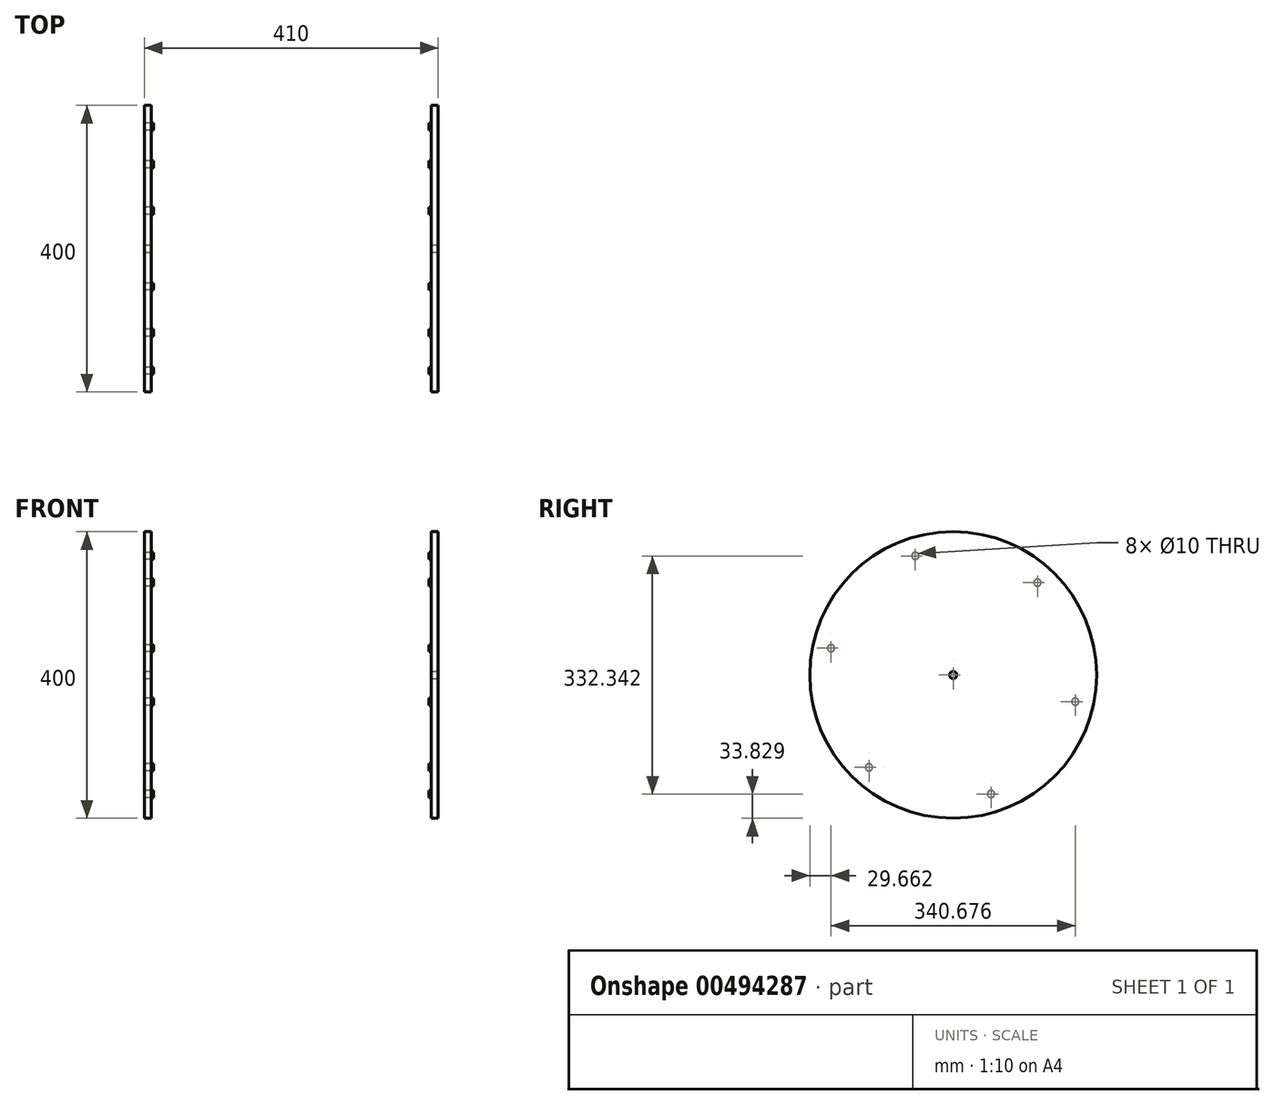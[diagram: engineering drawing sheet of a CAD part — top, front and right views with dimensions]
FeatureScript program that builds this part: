
annotation { "Feature Type Name" : "Feature", "Feature Type Description" : "" }
export const myFeature = defineFeature(function(context is Context, id is Id, definition is map)
    precondition{}
    {
        {
            var Q0;
            Q0=qCreatedBy(makeId("Right.planeOp"),FACE);
            var sketch = newSketch(context, id + "F0", { "sketchPlane" : qUnion([Q0])});
            skCircle(sketch, "E0", {"center": v(0, 0) * mm, "radius": 200 * mm});
            skCircle(sketch, "E1", {"center": v(52.86, -166.17) * mm, "radius": 5 * mm});
            skCircle(sketch, "E2.1.0", {"center": v(170.34, -37.3) * mm, "radius": 5 * mm});
            skCircle(sketch, "E2.2.0", {"center": v(117.48, 128.86) * mm, "radius": 5 * mm});
            skCircle(sketch, "E2.3.0", {"center": v(-52.86, 166.17) * mm, "radius": 5 * mm});
            skCircle(sketch, "E2.4.0", {"center": v(-170.34, 37.3) * mm, "radius": 5 * mm});
            skCircle(sketch, "E2.5.0", {"center": v(-117.48, -128.86) * mm, "radius": 5 * mm});
            skSolve(sketch);
        }
        {
            var Q0;
            Q0=makeQuery(id+"F0.imprint","IMPRINT",FACE,{"disambiguationData":[TD([[makeQuery(id+"F0.imprint","IMPRINT",EDGE,{"derivedFrom":sQuery(id+"F0.wireOp",EDGE,"E1")}),1.0]])]});
            var Q1;
            Q1=makeQuery(id+"F0.imprint","IMPRINT",FACE,{"disambiguationData":[TD([[makeQuery(id+"F0.imprint","IMPRINT",EDGE,{"derivedFrom":sQuery(id+"F0.wireOp",EDGE,"E2.5.0")}),1.0]])]});
            var Q2;
            Q2=makeQuery(id+"F0.imprint","IMPRINT",FACE,{"disambiguationData":[TD([[makeQuery(id+"F0.imprint","IMPRINT",EDGE,{"derivedFrom":sQuery(id+"F0.wireOp",EDGE,"E2.4.0")}),1.0]])]});
            var Q3;
            Q3=makeQuery(id+"F0.imprint","IMPRINT",FACE,{"disambiguationData":[TD([[makeQuery(id+"F0.imprint","IMPRINT",EDGE,{"derivedFrom":sQuery(id+"F0.wireOp",EDGE,"E2.3.0")}),1.0]])]});
            var Q4;
            Q4=makeQuery(id+"F0.imprint","IMPRINT",FACE,{"disambiguationData":[TD([[makeQuery(id+"F0.imprint","IMPRINT",EDGE,{"derivedFrom":sQuery(id+"F0.wireOp",EDGE,"E2.1.0")}),1.0]])]});
            var Q5;
            Q5=makeQuery(id+"F0.imprint","IMPRINT",FACE,{"disambiguationData":[TD([[makeQuery(id+"F0.imprint","IMPRINT",EDGE,{"derivedFrom":sQuery(id+"F0.wireOp",EDGE,"E2.2.0")}),1.0]])]});
            extrude(context, id + "F1", {"entities" : qUnion([Q0, Q1, Q2, Q3, Q4, Q5]), "depth" : 400 * mm});
        }
        {
            var Q0;
            Q0 = qSketchRegion(id + "F0", true);
            extrude(context, id + "F2", {"entities" : qUnion([Q0]), "depth" : 10 * mm});
        }
        {
            var Q0;
            Q0=makeQuery(id+"F1.opExtrude","CAP_FACE",FACE,{"disambiguationData":[OSD([sQuery(id+"F0.wireOp",EDGE,"E2.1.0")])],"isStart":false});
            var sketch = newSketch(context, id + "F3", { "sketchPlane" : qUnion([Q0])});
            skCircle(sketch, "E3", {"center": v(0, 0) * mm, "radius": 200 * mm});
            skSolve(sketch);
        }
        {
            var Q0;
            Q0 = qSketchRegion(id + "F3", true);
            extrude(context, id + "F4", {"entities" : qUnion([Q0]), "operationType" : NewBodyOperationType.ADD, "depth" : 10 * mm});
        }
        {
            var Q0;
            Q0=makeQuery(id+"F4.opExtrude","CAP_FACE",FACE,{"disambiguationData":[OSD([sQuery(id+"F3.wireOp",EDGE,"E3")])],"isStart":false});
            var sketch = newSketch(context, id + "F5", { "sketchPlane" : qUnion([Q0])});
            skCircle(sketch, "E4", {"center": v(0, 0) * mm, "radius": 5 * mm});
            skSolve(sketch);
        }
        {
            var Q0;
            Q0 = qSketchRegion(id + "F5", true);
            extrude(context, id + "F6", {"entities" : qUnion([Q0]), "operationType" : NewBodyOperationType.REMOVE, "oppositeDirection" : true, "depth" : 3000 * mm});
        }
        {
            var Q0;
            Q0=qCreatedBy(makeId("Top.planeOp"),FACE);
            var sketch = newSketch(context, id + "F7", { "sketchPlane" : qUnion([Q0])});
            skLineSegment(sketch, "E5.bottom", {"start": v(13, 554.52) * mm, "end": v(397, 554.52) * mm});
            skLineSegment(sketch, "E5.top", {"start": v(13, -45.48) * mm, "end": v(397, -45.48) * mm});
            skLineSegment(sketch, "E5.left", {"start": v(13, 554.52) * mm, "end": v(13, -45.48) * mm});
            skLineSegment(sketch, "E5.right", {"start": v(397, 554.52) * mm, "end": v(397, -45.48) * mm});
            skLineSegment(sketch, "E6.top", {"start": v(13, -267.99) * mm, "end": v(397, -267.99) * mm});
            skLineSegment(sketch, "E6.left", {"start": v(13, -45.48) * mm, "end": v(13, -267.99) * mm});
            skLineSegment(sketch, "E6.right", {"start": v(397, -45.48) * mm, "end": v(397, -267.99) * mm});
            skSolve(sketch);
        }
        {
            var Q0;
            Q0 = qSketchRegion(id + "F7", true);
            extrude(context, id + "F8", {"entities" : qUnion([Q0]), "operationType" : NewBodyOperationType.REMOVE, "endBound" : BoundingType.SYMMETRIC, "oppositeDirection" : true, "depth" : 400 * mm});
        }
    });
